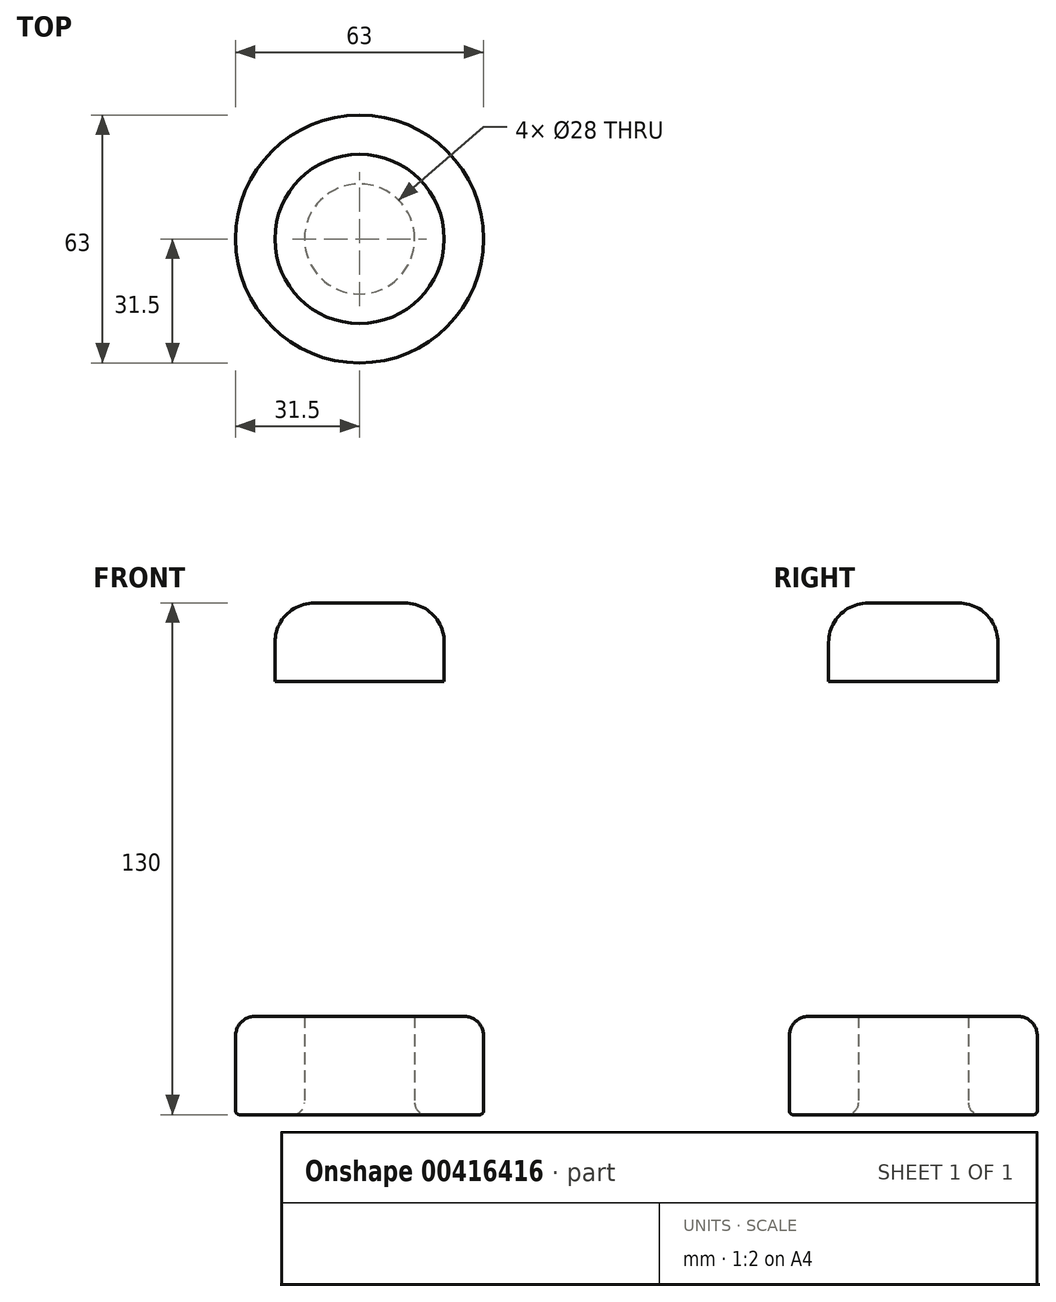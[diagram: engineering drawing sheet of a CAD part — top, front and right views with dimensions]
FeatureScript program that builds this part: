
annotation { "Feature Type Name" : "Feature", "Feature Type Description" : "" }
export const myFeature = defineFeature(function(context is Context, id is Id, definition is map)
    precondition{}
    {
        {
            var Q0;
            Q0=qCreatedBy(makeId("Front.planeOp"),FACE);
            var sketch = newSketch(context, id + "F0", { "sketchPlane" : qUnion([Q0])});
            skLineSegment(sketch, "E0.bottom", {"start": v(17, 0) * mm, "end": v(30.5, 0) * mm});
            skLineSegment(sketch, "E0.top", {"start": v(14, 25) * mm, "end": v(26.5, 25) * mm});
            skLineSegment(sketch, "E0.left", {"start": v(14, 3) * mm, "end": v(14, 25) * mm});
            skLineSegment(sketch, "E0.right", {"start": v(31.5, 1) * mm, "end": v(31.5, 20) * mm});
            skLineSegment(sketch, "E1.bottom", {"start": v(14, 25) * mm, "end": v(21.5, 25) * mm});
            skLineSegment(sketch, "E1.top", {"start": v(14, 110) * mm, "end": v(21.5, 110) * mm});
            skLineSegment(sketch, "E1.left", {"start": v(14, 25) * mm, "end": v(14, 110) * mm});
            skLineSegment(sketch, "E1.right", {"start": v(21.5, 25) * mm, "end": v(21.5, 110) * mm});
            skLineSegment(sketch, "E2.bottom", {"start": v(21.5, 110) * mm, "end": v(0, 110) * mm});
            skLineSegment(sketch, "E2.top", {"start": v(11.5, 130) * mm, "end": v(0, 130) * mm});
            skLineSegment(sketch, "E2.left", {"start": v(21.5, 110) * mm, "end": v(21.5, 120) * mm});
            skLineSegment(sketch, "E2.right", {"start": v(0, 110) * mm, "end": v(0, 130) * mm});
            skPoint(sketch, "E3.visualSharp", {"position": v(31.5, 0) * mm});
            skArc(sketch, "E3.filletArc", {"start": v(30.5, 0) * mm, "mid": v(31.2, 0.3) * mm, "end": v(31.5, 1) * mm});
            skPoint(sketch, "E4.visualSharp", {"position": v(31.5, 25) * mm});
            skArc(sketch, "E4.filletArc", {"start": v(31.5, 20) * mm, "mid": v(30.04, 23.54) * mm, "end": v(26.5, 25) * mm});
            skPoint(sketch, "E5.visualSharp", {"position": v(14, 0) * mm});
            skArc(sketch, "E5.filletArc", {"start": v(14, 3) * mm, "mid": v(14.88, 0.88) * mm, "end": v(17, 0) * mm});
            skPoint(sketch, "E6.visualSharp", {"position": v(21.5, 130) * mm});
            skArc(sketch, "E6.filletArc", {"start": v(21.5, 120) * mm, "mid": v(18.57, 127.07) * mm, "end": v(11.5, 130) * mm});
            skSolve(sketch);
        }
        {
            var Q0;
            Q0=makeQuery(id+"F0.imprint","IMPRINT",FACE,{"disambiguationData":[TD([[makeQuery(id+"F0.imprint","IMPRINT",EDGE,{"derivedFrom":sQuery(id+"F0.wireOp",EDGE,"E1.bottom")}),1.0]])]});
            var Q1;
            Q1=makeQuery(id+"F0.imprint","IMPRINT",FACE,{"disambiguationData":[TD([[makeQuery(id+"F0.imprint","IMPRINT",EDGE,{"derivedFrom":sQuery(id+"F0.wireOp",EDGE,"E0.bottom")}),1.0]])]});
            var Q2;
            Q2=makeQuery(id+"F0.imprint","IMPRINT",FACE,{"disambiguationData":[TD([[makeQuery(id+"F0.imprint","IMPRINT",EDGE,{"derivedFrom":sQuery(id+"F0.wireOp",EDGE,"E2.top")}),1.0]])]});
            var Q3;
            Q3=sQuery(id+"F0.wireOp",EDGE,"E2.right");
            revolve(context, id + "F1", {"entities" : qUnion([Q0, Q1, Q2]), "axis" : qUnion([Q3]), "revolveType" : RevolveType.FULL});
        }
    });
